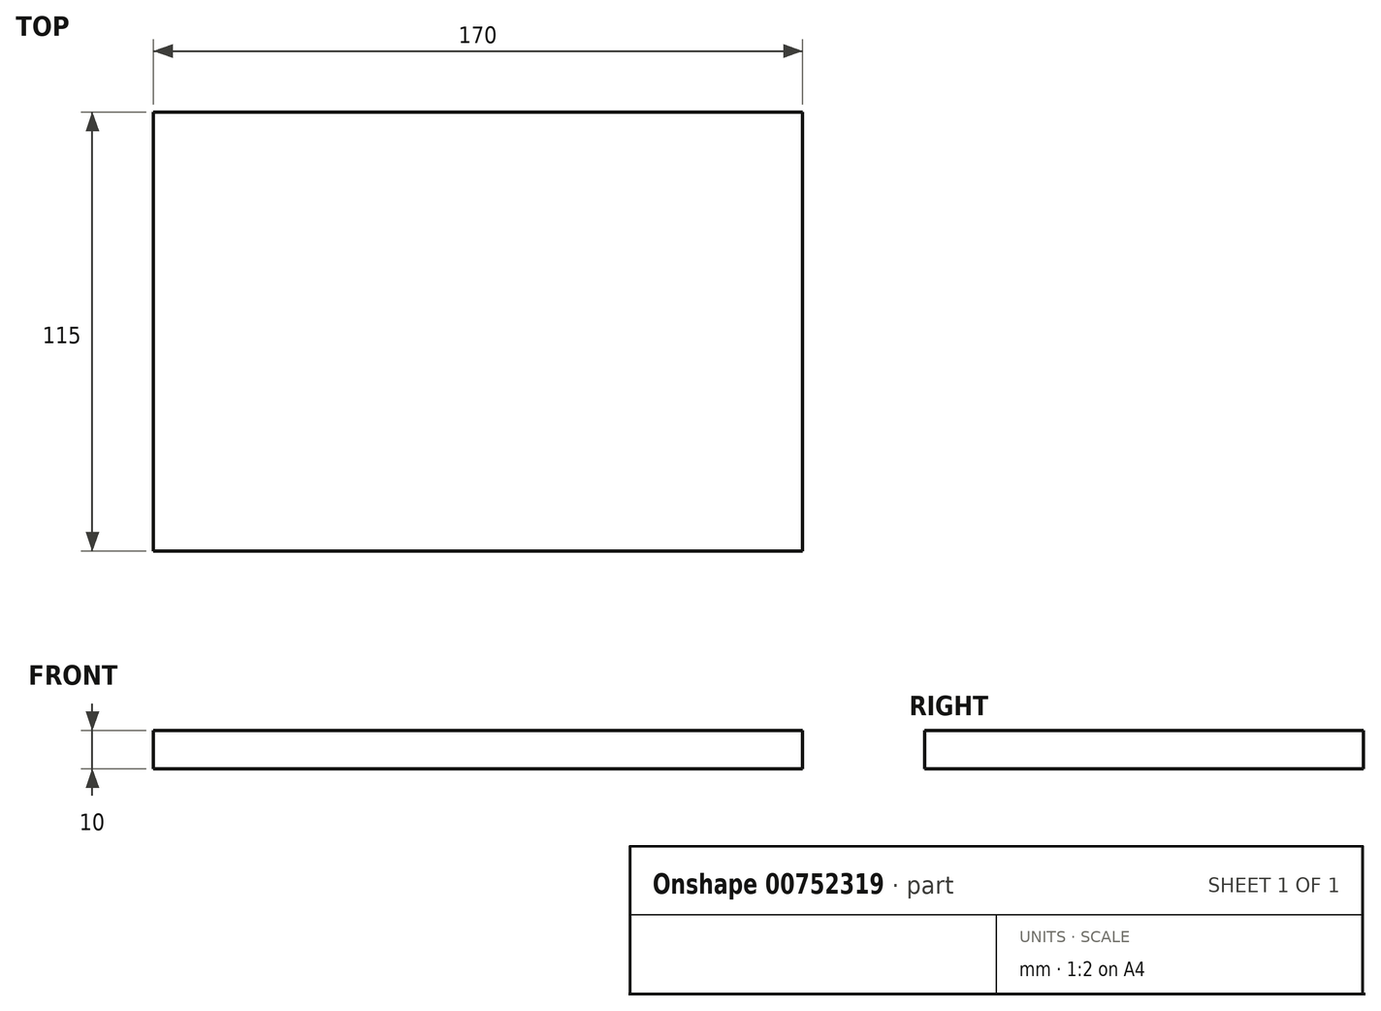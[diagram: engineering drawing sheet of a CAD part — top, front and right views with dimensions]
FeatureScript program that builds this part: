
annotation { "Feature Type Name" : "Feature", "Feature Type Description" : "" }
export const myFeature = defineFeature(function(context is Context, id is Id, definition is map)
    precondition{}
    {
        {
            var Q0;
            Q0=qCreatedBy(makeId("Top.planeOp"),FACE);
            var sketch = newSketch(context, id + "F0", { "sketchPlane" : qUnion([Q0])});
            skLineSegment(sketch, "E0.bottom", {"start": v(85, 57.5) * mm, "end": v(-85, 57.5) * mm});
            skLineSegment(sketch, "E0.top", {"start": v(85, -57.5) * mm, "end": v(-85, -57.5) * mm});
            skLineSegment(sketch, "E0.left", {"start": v(85, 57.5) * mm, "end": v(85, -57.5) * mm});
            skLineSegment(sketch, "E0.right", {"start": v(-85, 57.5) * mm, "end": v(-85, -57.5) * mm});
            skPoint(sketch, "E0.middle", {"position": v(0, 0) * mm});
            skSolve(sketch);
        }
        {
            var Q0;
            Q0 = qSketchRegion(id + "F0", true);
            extrude(context, id + "F1", {"entities" : qUnion([Q0]), "depth" : 10 * mm, "offsetDistance" : 25 * mm});
        }
    });
